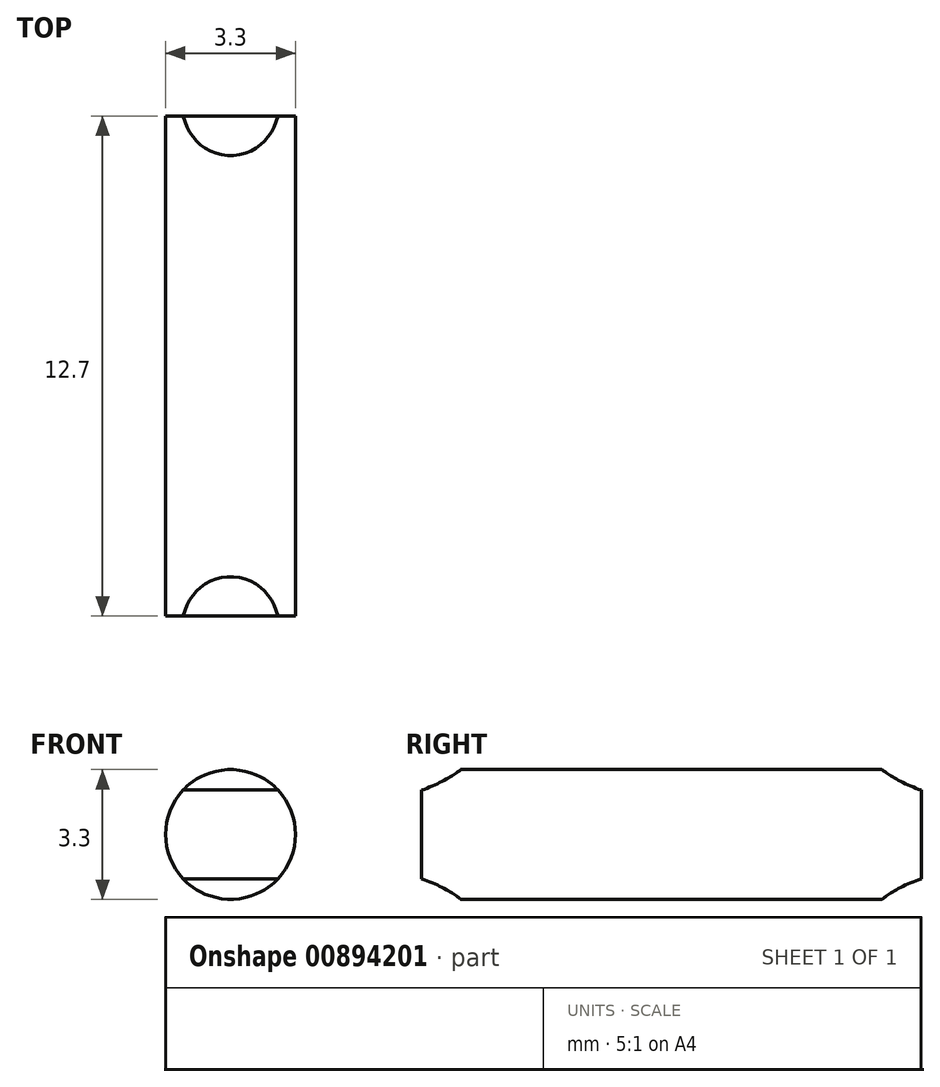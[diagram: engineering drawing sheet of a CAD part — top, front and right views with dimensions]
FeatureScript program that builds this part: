
annotation { "Feature Type Name" : "Feature", "Feature Type Description" : "" }
export const myFeature = defineFeature(function(context is Context, id is Id, definition is map)
    precondition{}
    {
        {
            var Q0;
            Q0=qCreatedBy(makeId("Right.planeOp"),FACE);
            var sketch = newSketch(context, id + "F0", { "sketchPlane" : qUnion([Q0])});
            skLineSegment(sketch, "E0", {"start": v(0, 0) * mm, "end": v(0, 1.65) * mm});
            skLineSegment(sketch, "E1", {"start": v(0, 1.65) * mm, "end": v(12.7, 1.65) * mm});
            skLineSegment(sketch, "E2", {"start": v(12.7, 1.65) * mm, "end": v(12.7, 0) * mm});
            skLineSegment(sketch, "E3", {"start": v(12.7, 0) * mm, "end": v(0, 0) * mm});
            skSolve(sketch);
        }
        {
            var Q0;
            Q0=makeQuery(id+"F0.imprint","IMPRINT",FACE,{"disambiguationData":[TD([[makeQuery(id+"F0.imprint","IMPRINT",EDGE,{"derivedFrom":sQuery(id+"F0.wireOp",EDGE,"E0")}),-1.0]])]});
            var Q1;
            Q1=sQuery(id+"F0.wireOp",EDGE,"E3");
            revolve(context, id + "F1", {"surfaceOperationType" : NewSurfaceOperationType.NEW, "entities" : qUnion([Q0]), "axis" : qUnion([Q1]), "revolveType" : RevolveType.FULL});
        }
        {
            var Q0;
            Q0=qCreatedBy(makeId("Right.planeOp"),FACE);
            var sketch = newSketch(context, id + "F2", { "sketchPlane" : qUnion([Q0])});
            skArc(sketch, "E4", {"start": v(0, 1.13) * mm, "mid": v(0.52, 1.35) * mm, "end": v(1, 1.65) * mm});
            skLineSegment(sketch, "E5", {"start": v(0, 0) * mm, "end": v(0, 1.13) * mm, "construction": true});
            skLineSegment(sketch, "E6", {"start": v(0, 1.13) * mm, "end": v(0, 1.65) * mm});
            skLineSegment(sketch, "E7", {"start": v(0, 1.65) * mm, "end": v(1, 1.65) * mm});
            skLineSegment(sketch, "E8", {"start": v(0, 0) * mm, "end": v(6.35, 0) * mm, "construction": true});
            skLineSegment(sketch, "E9", {"start": v(6.35, 0) * mm, "end": v(6.35, 1.65) * mm, "construction": true});
            skLineSegment(sketch, "E10.MirrorCS", {"start": v(12.7, 1.13) * mm, "end": v(12.7, 1.65) * mm});
            skLineSegment(sketch, "E11.MirrorCS", {"start": v(12.7, 1.65) * mm, "end": v(11.7, 1.65) * mm});
            skArc(sketch, "E12.MirrorCS", {"start": v(12.7, 1.13) * mm, "mid": v(12.18, 1.35) * mm, "end": v(11.7, 1.65) * mm});
            skLineSegment(sketch, "E13.MirrorCS", {"start": v(6.35, 0) * mm, "end": v(6.35, -1.65) * mm, "construction": true});
            skLineSegment(sketch, "E14.MirrorCS", {"start": v(12.7, -1.65) * mm, "end": v(11.7, -1.65) * mm});
            skArc(sketch, "E15.MirrorCS", {"start": v(12.7, -1.13) * mm, "mid": v(12.18, -1.35) * mm, "end": v(11.7, -1.65) * mm});
            skArc(sketch, "E16.MirrorCS", {"start": v(0, -1.13) * mm, "mid": v(0.52, -1.35) * mm, "end": v(1, -1.65) * mm});
            skLineSegment(sketch, "E17.MirrorCS", {"start": v(0, -1.65) * mm, "end": v(1, -1.65) * mm});
            skLineSegment(sketch, "E18.MirrorCS", {"start": v(0, -1.13) * mm, "end": v(0, -1.65) * mm});
            skLineSegment(sketch, "E19.MirrorCS", {"start": v(12.7, -1.13) * mm, "end": v(12.7, -1.65) * mm});
            skSolve(sketch);
        }
        {
            var Q0;
            Q0 = qSketchRegion(id + "F2", true);
            extrude(context, id + "F3", {"entities" : qUnion([Q0]), "operationType" : NewBodyOperationType.REMOVE, "oppositeDirection" : true, "depth" : 3.3 * mm, "offsetDistance" : 25 * mm, "symmetric" : true});
        }
    });
